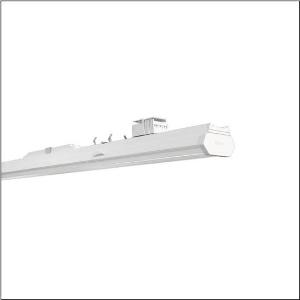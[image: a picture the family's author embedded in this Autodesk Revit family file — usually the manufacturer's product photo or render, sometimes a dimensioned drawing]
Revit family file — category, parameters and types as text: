
# Revit family: licross_r__21_protected_ho_52tp12mn4e5m_b3cb
name_source: partatom
category: Lighting Fixtures
units: mm (PartAtom-declared; Revit-internal decimal feet)

## family parameters
Cut with Voids When Loaded = No
Host = Face
Light Source = No
Part Type = Normal
Room Calculation Point = No
Round Connector Dimension = Use Diameter
Shared = No

## types (1)
- --- (1 x LED, 14780 lm, 83.2 W, 4000K)
    Apparent Load = 83 VA
    CIE Flux Codes = 70 91 97 98 100
    Color Rendering = 80
    Color Temperature = 4000K
    Default Elevation = 1800 mm
    Description = Licross® 21 Protected HO, luminaire insert, of sheet steel, galvanised, coil coated, white, length: 1.500mm, width: 90mm, height: 101mm, LED rated luminous flux: 14.790lm, light colour: 840, SDCM (Standard Deviation of Colour Matching)MacAdam ≤ 3 SDCM (initial), control gear: ON/OFF Multilumen, with plug, 3-pole, with phase selection, mains connection: 220..240V, AC, 50/60Hz, rated input power: 83W, internal wiring halogen-free, primary light control with lens, of plastic, primary optical cover: cover, of PMMA, light emission: direct distribution, primary light characteristic: symmetric, protection rating (complete): IP64, insulation class (complete): insulation class I (protective earthing), certification: CE, ENEC, VDE, UKCA, protection symbol: D if used in an environment with conductive dust loads with corresponding accessories, impact resistance: IK06, permissible ambient temperature for indoor applications: -35..+35°C, corresponds to IFS (International Featured Standards) requirements for safety and quality in the food industry, reducing of maximum allowable ambient temperature of 5°C with ceiling mounting, LABS conformity tested according to VDMA 24364:2018-05, packaging unit: 1 piece
    Height = 92 mm
    Lamp = 1 x LED
    Lamp Light Flux = 14780 lm
    Lamp Power = 83.2 W
    Lamp count = 1
    Length = 1500 mm
    Luminous efficacy = 178 lm/W
    Manufacturer = Siteco
    ModVariant = No
    Model = 52TP12MN4E5M
    Mounting Place = Ceiling
    Mounting Type = Pendant
    Number of Poles = 1
    OnlyDefault = Yes
    Power Factor = 1
    Product Name = Licross® 21 Protected HO
    Product group = luminaire insert | ceiling pendant
    ProductGroupID = 901
    Protection Class = Protection class I
    Protection Degree = IP 64
    RLX_Detail_Level = 1
    RLX_Emergency_Light_Flux = 0 lm
    RLX_Emergency_Type = 0
    RLX_Emergency_Type_DB = No
    RlxData = <blob elided: 22137 chars, md5=32edb06d>
    Socket = socket
    Standby Power = 0 W
    System Light Flux = 14780 lm
    System Power = 83 W
    Type Comments = factory setting: luminous flux: 100 % | (A | C | E) | 195 mA
    Type Image = l_1256148.jpg
    URL = http://relux.com
    VarID = @adj_113061
    Voltage = 0 V
    Weight = 0.00 kg
    Width = 88 mm

## geometry (parser evidence)
native form markers: Blend x4, Sweep x11
no freeform markers — native parametric forms only
